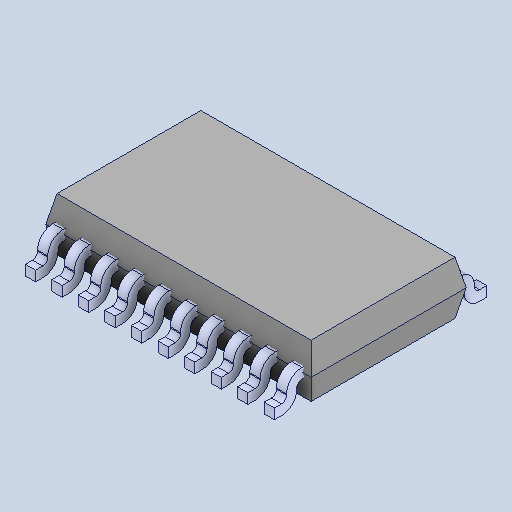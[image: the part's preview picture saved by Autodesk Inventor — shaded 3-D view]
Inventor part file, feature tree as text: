
AUTODESK INVENTOR PART (.ipt)
format: ipt  version: 2023.1 (Build 271208000, 208)  size: 297,984 bytes
history: native  units: in
note: dims shown in document units (in); Inventor stores cm internally (conversion verified against a paired STEP export)
features: other x10, mirror x10, fillet x1
ambient origin geometry x8: Origin, YZ Plane, XZ Plane, XY Plane, X Axis, Y Axis, Z Axis, Center Point
bodies: Solid1 (feature_tree), Solid2 (feature_tree), Solid3 (feature_tree), Solid4 (feature_tree), Solid5 (feature_tree), Solid6 (feature_tree), Solid7 (feature_tree), Solid8 (feature_tree), Solid9 (feature_tree), Solid10 (feature_tree), Solid11 (feature_tree), Solid12 (feature_tree), Solid13 (feature_tree), Solid14 (feature_tree), Solid15 (feature_tree), Solid16 (feature_tree), Solid17 (feature_tree), Solid18 (feature_tree), Solid19 (feature_tree), Solid20 (feature_tree), Solid21 (feature_tree)
feature tree (21):
  other  "Boss-Extrude1"
  fillet  "Fillet2"  [1 undecoded]
  other  "LPattern2[1]"
  other  "LPattern2[2]"
  other  "LPattern2[3]"
  other  "LPattern2[4]"
  other  "LPattern2[5]"
  other  "LPattern2[6]"
  other  "LPattern2[7]"
  other  "LPattern2[8]"
  other  "LPattern2[9]"
  mirror  "Mirror2[1]"
  mirror  "Mirror2[2]"
  mirror  "Mirror2[3]"
  mirror  "Mirror2[4]"
  mirror  "Mirror2[5]"
  mirror  "Mirror2[6]"
  mirror  "Mirror2[7]"
  mirror  "Mirror2[8]"
  mirror  "Mirror2[9]"
  mirror  "Mirror2[10]"
note: 1 required parameter value undecoded (feature->parameter linkage not recoverable at this tier; creation-order binding heuristic only, values carry confidence <= 0.55)
